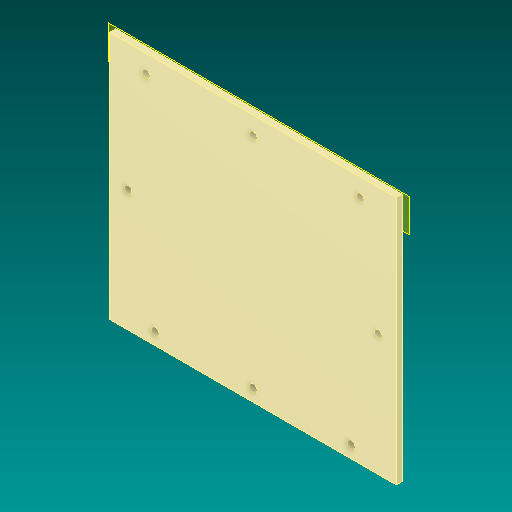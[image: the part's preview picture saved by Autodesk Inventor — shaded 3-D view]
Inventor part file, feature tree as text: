
AUTODESK INVENTOR PART (.ipt)
format: ipt  version: 2019 (Build 230136000, 136)  size: 139,776 bytes
history: native  units: mm
features: reference x16, extrude x5, sketch x5, other x5, plane x1
ambient origin geometry x8: Origin, YZ Plane, XZ Plane, XY Plane, X Axis, Y Axis, Z Axis, Center Point
bodies: Solid1 (feature_tree)
feature tree (32):
  plane  "Work Plane1"
  extrude  "Extrusion1"  Depth=2.0mm
  extrude  "Extrusion2"  Depth=2.5mm
  extrude  "Extrusion3"  Depth=2.5mm
  extrude  "Extrusion4"  Depth=2.0mm TaperAngle=0.0deg
  extrude  "Extrusion5"  Depth=2.0mm TaperAngle=0.0deg
  sketch  "Sketch1"  dims[d0=2.0mm d1=0.0mm d2=2.5mm]
  reference  "Reference1"
  reference  "Reference2"
  reference  "Reference3"
  reference  "Reference4"
  reference  "Reference5"
  reference  "Reference6"
  reference  "Reference7"
  reference  "Reference8"
  reference  "Reference9"
  reference  "Reference10"
  reference  "Reference11"
  reference  "Reference12"
  reference  "Reference13"
  sketch  "Sketch2"  dims[d3=2.5mm d4=2.5mm]
  sketch  "Sketch3"  dims[d5=2.5mm d6=2.5mm]
  sketch  "Sketch4"  dims[d7=2.5mm d8=2.0mm d9=0.0mm]
  sketch  "Sketch5"  dims[d10=2.0mm d11=0.0mm d12=2.0mm d13=0.0mm d21=2.5mm d25=2.5mm d26=2.0mm d27=0.0mm]
  reference  "Reference14"
  reference  "Reference15"
  reference  "Reference16"
  other  "Ensamblaje Reloj LCD 16x2.iam"
  other  "Lateral Derecho:1"
  other  "Lado izquierdo:1"
  other  "Before:1"
  other  "Down:1"
